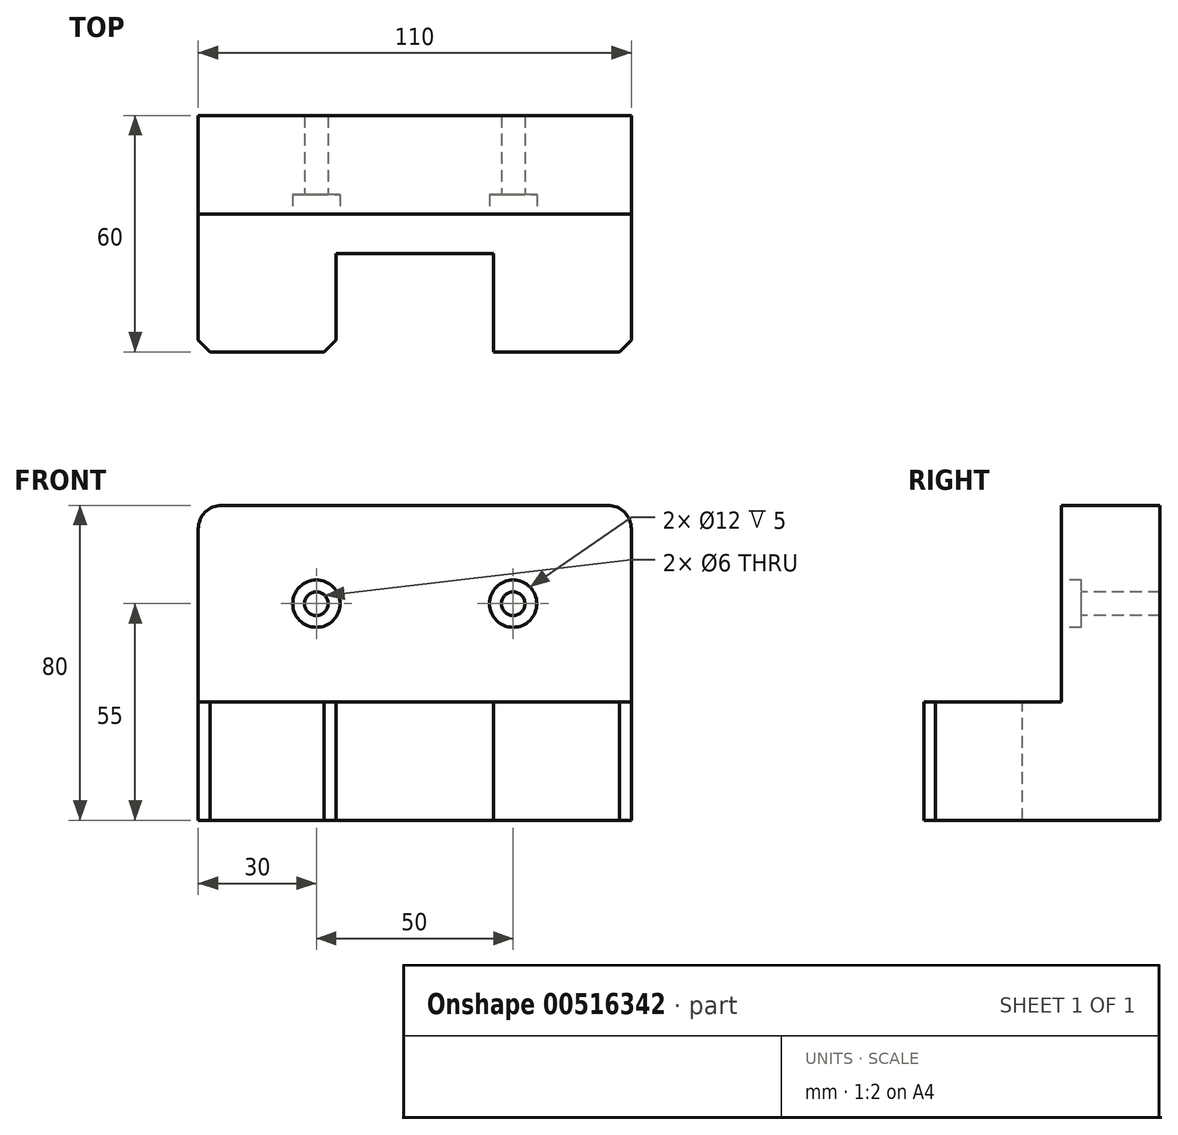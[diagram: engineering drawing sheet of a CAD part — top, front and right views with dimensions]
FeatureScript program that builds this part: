
annotation { "Feature Type Name" : "Feature", "Feature Type Description" : "" }
export const myFeature = defineFeature(function(context is Context, id is Id, definition is map)
    precondition{}
    {
        {
            var Q0;
            Q0=qCreatedBy(makeId("Front.planeOp"),FACE);
            var sketch = newSketch(context, id + "F0", { "sketchPlane" : qUnion([Q0])});
            skLineSegment(sketch, "E0.bottom", {"start": v(55, -40) * mm, "end": v(-55, -40) * mm});
            skLineSegment(sketch, "E0.top", {"start": v(55, 40) * mm, "end": v(-55, 40) * mm});
            skLineSegment(sketch, "E0.left", {"start": v(55, -40) * mm, "end": v(55, 40) * mm});
            skLineSegment(sketch, "E0.right", {"start": v(-55, -40) * mm, "end": v(-55, 40) * mm});
            skPoint(sketch, "E0.middle", {"position": v(0, 0) * mm});
            skSolve(sketch);
        }
        {
            var Q0;
            Q0 = qSketchRegion(id + "F0", true);
            extrude(context, id + "F1", {"entities" : qUnion([Q0]), "depth" : 60 * mm, "offsetDistance" : 25 * mm});
        }
        {
            var Q0;
            Q0=makeQuery(id+"F1.opExtrude","CAP_FACE",FACE,{"disambiguationData":[OSD([sQuery(id+"F0.wireOp",EDGE,"E0.bottom"),sQuery(id+"F0.wireOp",EDGE,"E0.top"),sQuery(id+"F0.wireOp",EDGE,"E0.left"),sQuery(id+"F0.wireOp",EDGE,"E0.right")])],"isStart":false});
            var sketch = newSketch(context, id + "F2", { "sketchPlane" : qUnion([Q0])});
            skLineSegment(sketch, "E1.bottom", {"start": v(-55, 40) * mm, "end": v(55, 40) * mm});
            skLineSegment(sketch, "E1.top", {"start": v(-55, -10) * mm, "end": v(55, -10) * mm});
            skLineSegment(sketch, "E1.left", {"start": v(-55, 40) * mm, "end": v(-55, -10) * mm});
            skLineSegment(sketch, "E1.right", {"start": v(55, 40) * mm, "end": v(55, -10) * mm});
            skSolve(sketch);
        }
        {
            var Q0;
            Q0 = qSketchRegion(id + "F2", true);
            extrude(context, id + "F3", {"entities" : qUnion([Q0]), "operationType" : NewBodyOperationType.REMOVE, "oppositeDirection" : true, "depth" : 35 * mm, "offsetDistance" : 25 * mm});
        }
        {
            var Q0;
            Q0=makeQuery(id+"F1.opExtrude","SWEPT_EDGE",EDGE,{"disambiguationData":[OSD([sQuery(id+"F0.wireOp",EDGE,"E0.top"),sQuery(id+"F0.wireOp",EDGE,"E0.left")])]});
            var Q1;
            Q1=makeQuery(id+"F1.opExtrude","SWEPT_EDGE",EDGE,{"disambiguationData":[OSD([sQuery(id+"F0.wireOp",EDGE,"E0.top"),sQuery(id+"F0.wireOp",EDGE,"E0.right")])]});
            fillet(context, id + "F4", {"entities" : qUnion([Q0, Q1]), "radius" : 6 * mm, "tangentPropagation" : true, "allowEdgeOverflow" : false});
        }
        {
            var Q0;
            Q0=makeQuery(id+"F3.boolean.opBoolean","COPY",FACE,{"derivedFrom":makeQuery(id+"F3.opExtrude","CAP_FACE",FACE,{"disambiguationData":[OSD([sQuery(id+"F2.wireOp",EDGE,"E1.bottom"),sQuery(id+"F2.wireOp",EDGE,"E1.top"),sQuery(id+"F2.wireOp",EDGE,"E1.left"),sQuery(id+"F2.wireOp",EDGE,"E1.right")])],"isStart":false})});
            var sketch = newSketch(context, id + "F5", { "sketchPlane" : qUnion([Q0])});
            skCircle(sketch, "E2", {"center": v(-25, 15) * mm, "radius": 6 * mm});
            skCircle(sketch, "E3", {"center": v(25, 15) * mm, "radius": 6 * mm});
            skSolve(sketch);
        }
        {
            var Q0;
            Q0 = qSketchRegion(id + "F5", true);
            extrude(context, id + "F6", {"entities" : qUnion([Q0]), "operationType" : NewBodyOperationType.REMOVE, "oppositeDirection" : true, "depth" : 5 * mm, "offsetDistance" : 25 * mm});
        }
        {
            var Q0;
            Q0=makeQuery(id+"F6.boolean.opBoolean","COPY",FACE,{"derivedFrom":makeQuery(id+"F6.opExtrude","CAP_FACE",FACE,{"disambiguationData":[OSD([sQuery(id+"F5.wireOp",EDGE,"E2")])],"isStart":false})});
            var sketch = newSketch(context, id + "F7", { "sketchPlane" : qUnion([Q0])});
            skCircle(sketch, "E4", {"center": v(-25, 15) * mm, "radius": 3 * mm});
            skCircle(sketch, "E5", {"center": v(25, 15) * mm, "radius": 3 * mm});
            skSolve(sketch);
        }
        {
            var Q0;
            Q0 = qSketchRegion(id + "F7", true);
            extrude(context, id + "F8", {"entities" : qUnion([Q0]), "operationType" : NewBodyOperationType.REMOVE, "endBound" : BoundingType.THROUGH_ALL, "oppositeDirection" : true, "depth" : 25 * mm, "offsetDistance" : 25 * mm});
        }
        {
            var Q0;
            Q0=makeQuery(id+"F3.boolean.opBoolean","COPY",FACE,{"derivedFrom":makeQuery(id+"F3.opExtrude","SWEPT_FACE",FACE,{"disambiguationData":[OSD([sQuery(id+"F2.wireOp",EDGE,"E1.top")])]})});
            var sketch = newSketch(context, id + "F9", { "sketchPlane" : qUnion([Q0])});
            skLineSegment(sketch, "E6.bottom", {"start": v(-20, -60) * mm, "end": v(20, -60) * mm});
            skLineSegment(sketch, "E6.top", {"start": v(-20, -35) * mm, "end": v(20, -35) * mm});
            skLineSegment(sketch, "E6.left", {"start": v(-20, -60) * mm, "end": v(-20, -35) * mm});
            skLineSegment(sketch, "E6.right", {"start": v(20, -60) * mm, "end": v(20, -35) * mm});
            skSolve(sketch);
        }
        {
            var Q0;
            Q0 = qSketchRegion(id + "F9", true);
            extrude(context, id + "F10", {"entities" : qUnion([Q0]), "operationType" : NewBodyOperationType.REMOVE, "endBound" : BoundingType.THROUGH_ALL, "oppositeDirection" : true, "depth" : 25 * mm, "offsetDistance" : 25 * mm});
        }
        {
            var Q0;
            Q0=makeQuery(id+"F1.opExtrude","CAP_EDGE",EDGE,{"disambiguationData":[OSD([sQuery(id+"F0.wireOp",EDGE,"E0.right")])],"isStart":false});
            var Q1;
            Q1=makeQuery(id+"F1.opExtrude","CAP_EDGE",EDGE,{"disambiguationData":[OSD([sQuery(id+"F0.wireOp",EDGE,"E0.left")])],"isStart":false});
            var Q2;
            Q2=makeQuery(id+"F10.boolean.opBoolean","COPY",EDGE,{"derivedFrom":makeQuery(id+"F10.opExtrude","SWEPT_EDGE",EDGE,{"disambiguationData":[OSD([sQuery(id+"F2.wireOp",EDGE,"E1.top"),sQuery(id+"F9.wireOp",EDGE,"E6.bottom"),sQuery(id+"F9.wireOp",EDGE,"E6.left")])]})});
            var Q3;
            Q3=makeQuery(id+"F10.boolean.opBoolean","COPY",EDGE,{"derivedFrom":makeQuery(id+"F10.opExtrude","SWEPT_EDGE",EDGE,{"disambiguationData":[OSD([sQuery(id+"F2.wireOp",EDGE,"E1.top"),sQuery(id+"F9.wireOp",EDGE,"E6.bottom"),sQuery(id+"F9.wireOp",EDGE,"E6.right")])]})});
            chamfer(context, id + "F11", {"entities" : qUnion([Q0, Q1, Q2, Q3]), "chamferType" : ChamferType.OFFSET_ANGLE, "width" : 3 * mm, "oppositeDirection" : false, "angle" : 45 * degree, "tangentPropagation" : true});
        }
    });
